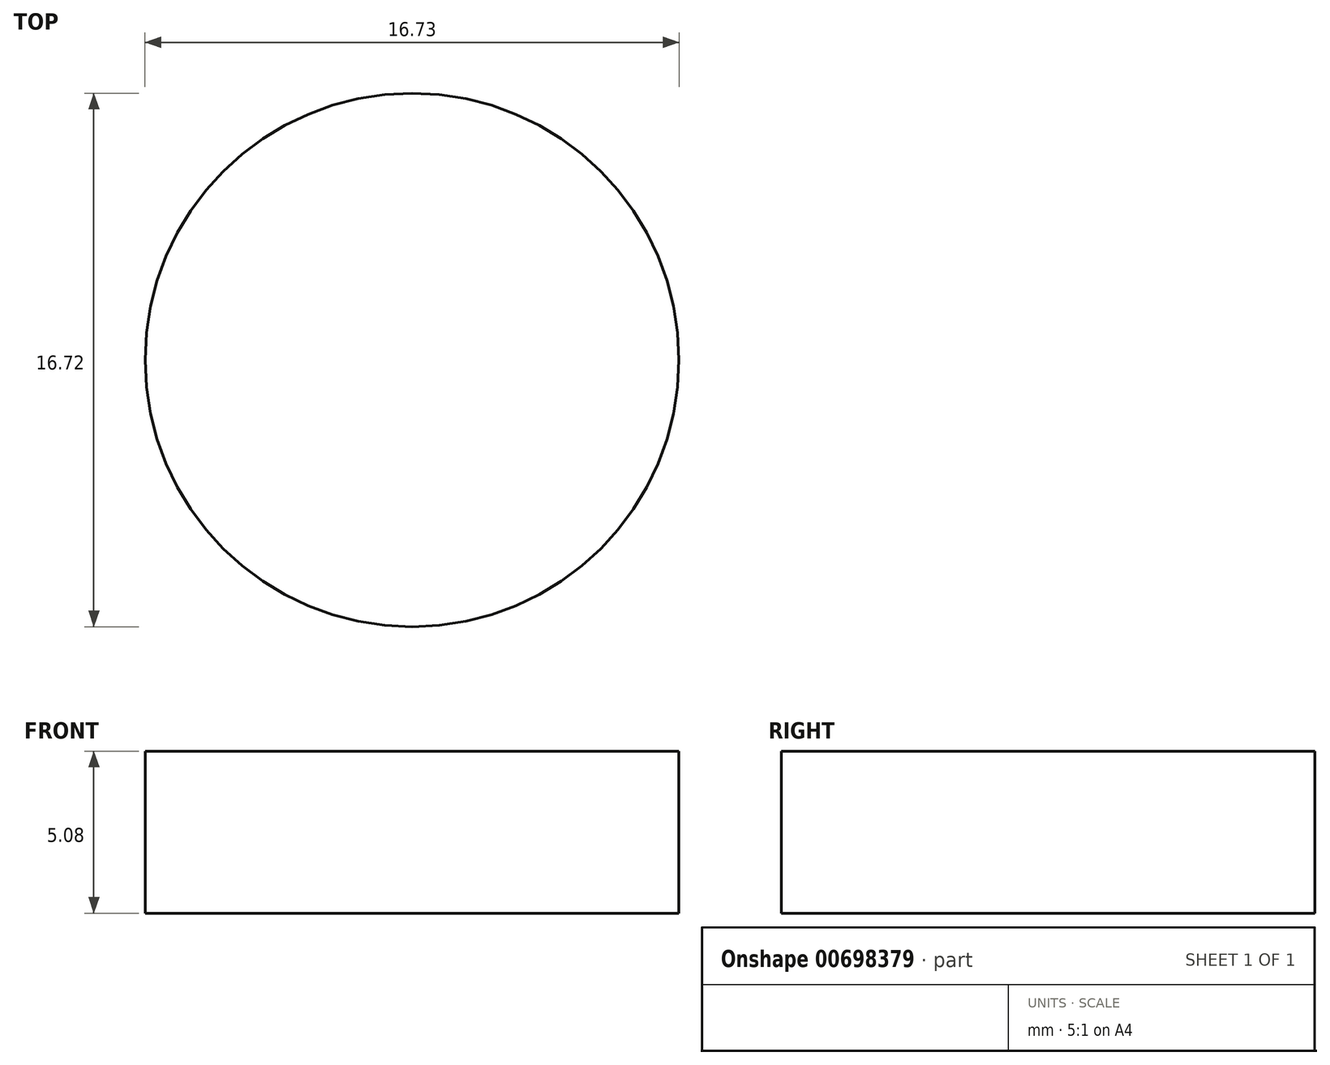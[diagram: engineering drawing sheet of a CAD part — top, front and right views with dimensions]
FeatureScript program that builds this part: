
annotation { "Feature Type Name" : "Feature", "Feature Type Description" : "" }
export const myFeature = defineFeature(function(context is Context, id is Id, definition is map)
    precondition{}
    {
        {
            var Q0;
            Q0=qCreatedBy(makeId("Top.planeOp"),FACE);
            var sketch = newSketch(context, id + "F0", { "sketchPlane" : qUnion([Q0])});
            skCircle(sketch, "E0", {"center": v(-9, -6.3) * mm, "radius": 8.36 * mm});
            skSolve(sketch);
        }
        {
            var Q0;
            Q0=makeQuery(id+"F0.imprint","IMPRINT",FACE,{"disambiguationData":[TD([[makeQuery(id+"F0.imprint","IMPRINT",EDGE,{"derivedFrom":sQuery(id+"F0.wireOp",EDGE,"E0")}),1.0]])]});
            extrude(context, id + "F1", {"entities" : qUnion([Q0]), "depth" : 5.08 * mm, "offsetDistance" : 25.4 * mm});
        }
    });
